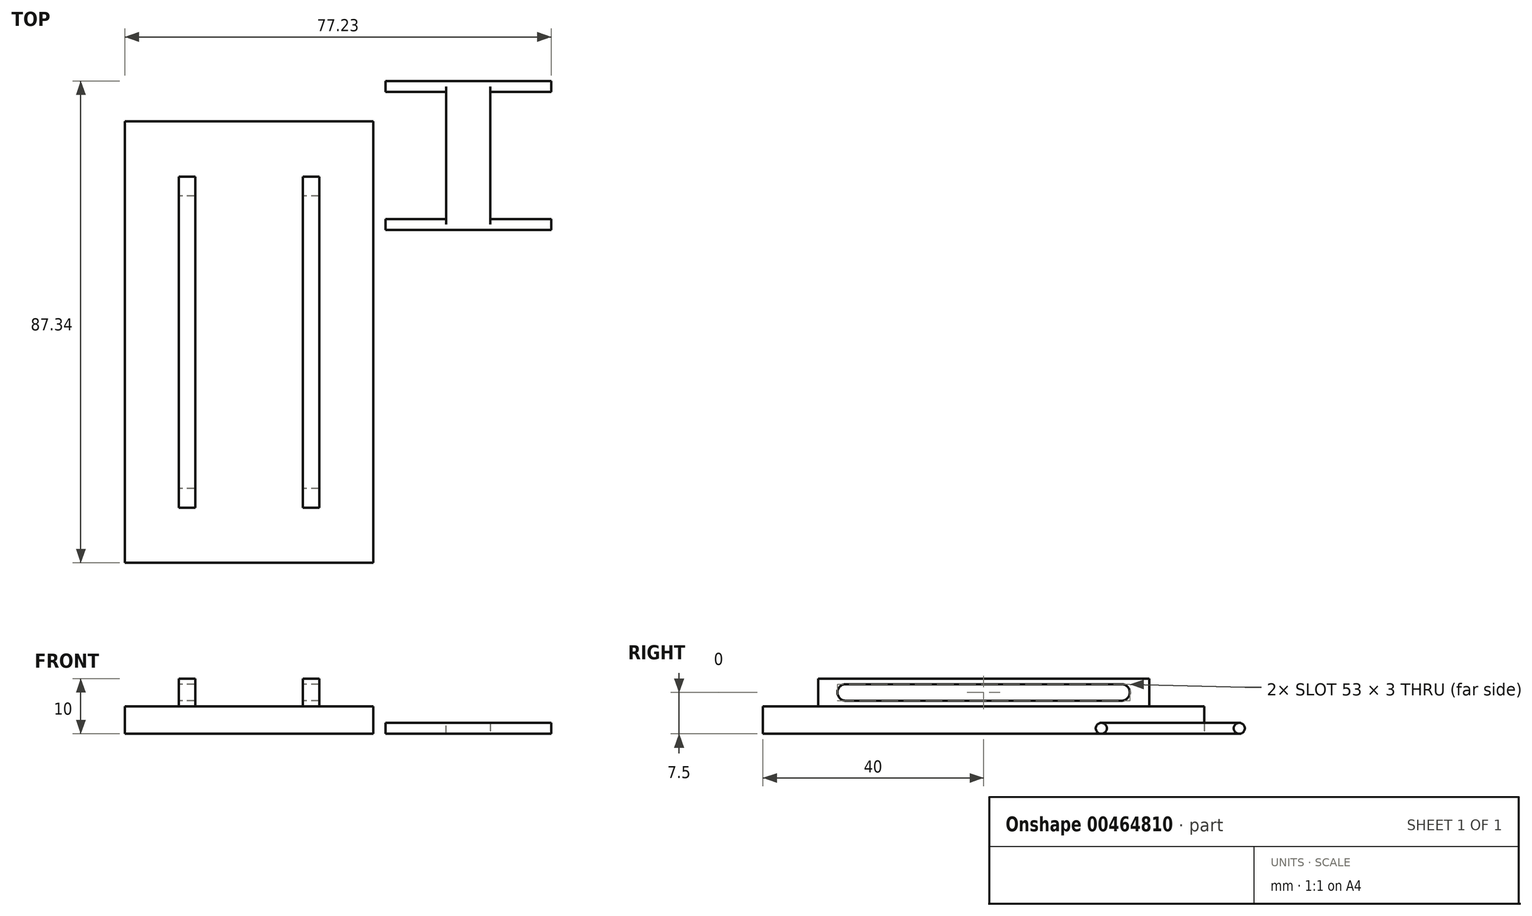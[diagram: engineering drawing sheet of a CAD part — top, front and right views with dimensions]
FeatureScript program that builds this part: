
annotation { "Feature Type Name" : "Feature", "Feature Type Description" : "" }
export const myFeature = defineFeature(function(context is Context, id is Id, definition is map)
    precondition{}
    {
        {
            var Q0;
            Q0=qCreatedBy(makeId("Top.planeOp"),FACE);
            var sketch = newSketch(context, id + "F0", { "sketchPlane" : qUnion([Q0])});
            skLineSegment(sketch, "E0.bottom", {"start": v(22.5, 40) * mm, "end": v(-22.5, 40) * mm});
            skLineSegment(sketch, "E0.top", {"start": v(22.5, -40) * mm, "end": v(-22.5, -40) * mm});
            skLineSegment(sketch, "E0.left", {"start": v(22.5, 40) * mm, "end": v(22.5, -40) * mm});
            skLineSegment(sketch, "E0.right", {"start": v(-22.5, 40) * mm, "end": v(-22.5, -40) * mm});
            skPoint(sketch, "E0.middle", {"position": v(0, 0) * mm});
            skSolve(sketch);
        }
        {
            var Q0;
            Q0=makeQuery(id+"F0.imprint","IMPRINT",FACE,{"disambiguationData":[TD([[makeQuery(id+"F0.imprint","IMPRINT",EDGE,{"derivedFrom":sQuery(id+"F0.wireOp",EDGE,"E0.bottom")}),1.0]])]});
            extrude(context, id + "F1", {"entities" : qUnion([Q0]), "depth" : 5 * mm});
        }
        {
            var Q0;
            Q0=makeQuery(id+"F1.opExtrude","CAP_FACE",FACE,{"disambiguationData":[OSD([sQuery(id+"F0.wireOp",EDGE,"E0.bottom"),sQuery(id+"F0.wireOp",EDGE,"E0.top"),sQuery(id+"F0.wireOp",EDGE,"E0.left"),sQuery(id+"F0.wireOp",EDGE,"E0.right")])],"isStart":false});
            var sketch = newSketch(context, id + "F2", { "sketchPlane" : qUnion([Q0])});
            skLineSegment(sketch, "E1", {"start": v(0, 0) * mm, "end": v(-22.5, 0) * mm, "construction": true});
            skPoint(sketch, "E2", {"position": v(-11.25, 0) * mm});
            skLineSegment(sketch, "E3.bottom", {"start": v(-9.75, 30) * mm, "end": v(-12.75, 30) * mm});
            skLineSegment(sketch, "E3.top", {"start": v(-9.75, -30) * mm, "end": v(-12.75, -30) * mm});
            skLineSegment(sketch, "E3.left", {"start": v(-9.75, 30) * mm, "end": v(-9.75, -30) * mm});
            skLineSegment(sketch, "E3.right", {"start": v(-12.75, 30) * mm, "end": v(-12.75, -30) * mm});
            skLineSegment(sketch, "E4", {"start": v(0, 0) * mm, "end": v(0, 3.84) * mm, "construction": true});
            skLineSegment(sketch, "E5.MirrorCS", {"start": v(9.75, 30) * mm, "end": v(9.75, -30) * mm});
            skLineSegment(sketch, "E6.MirrorCS", {"start": v(12.75, 30) * mm, "end": v(12.75, -30) * mm});
            skLineSegment(sketch, "E7.MirrorCS", {"start": v(9.75, 30) * mm, "end": v(12.75, 30) * mm});
            skLineSegment(sketch, "E8.MirrorCS", {"start": v(9.75, -30) * mm, "end": v(12.75, -30) * mm});
            skSolve(sketch);
        }
        {
            var Q0;
            Q0=makeQuery(id+"F2.imprint","IMPRINT",FACE,{"disambiguationData":[TD([[makeQuery(id+"F2.imprint","IMPRINT",EDGE,{"derivedFrom":sQuery(id+"F2.wireOp",EDGE,"E3.bottom")}),1.0]])]});
            var Q1;
            Q1=makeQuery(id+"F2.imprint","IMPRINT",FACE,{"disambiguationData":[TD([[makeQuery(id+"F2.imprint","IMPRINT",EDGE,{"derivedFrom":sQuery(id+"F2.wireOp",EDGE,"E5.MirrorCS")}),1.0]])]});
            extrude(context, id + "F3", {"entities" : qUnion([Q0, Q1]), "operationType" : NewBodyOperationType.ADD, "depth" : 5 * mm});
        }
        {
            var Q0;
            Q0=makeQuery(id+"F3.opExtrude","SWEPT_FACE",FACE,{"disambiguationData":[OSD([sQuery(id+"F2.wireOp",EDGE,"E3.right")])]});
            var sketch = newSketch(context, id + "F4", { "sketchPlane" : qUnion([Q0])});
            skLineSegment(sketch, "E9", {"start": v(-30, 7.5) * mm, "end": v(-25, 7.5) * mm, "construction": true});
            skCircle(sketch, "E10", {"center": v(-25, 7.5) * mm, "radius": 1.5 * mm});
            skLineSegment(sketch, "E11", {"start": v(-25, 7.5) * mm, "end": v(-25, 6) * mm, "construction": true});
            skLineSegment(sketch, "E12", {"start": v(-25, 6) * mm, "end": v(-25, 7.5) * mm, "construction": true});
            skLineSegment(sketch, "E13", {"start": v(-25, 7.5) * mm, "end": v(-25, 9) * mm, "construction": true});
            skLineSegment(sketch, "E14", {"start": v(0, 5) * mm, "end": v(0, 10) * mm, "construction": true});
            skLineSegment(sketch, "E15", {"start": v(-25, 9) * mm, "end": v(0, 9) * mm});
            skLineSegment(sketch, "E16", {"start": v(-25, 6) * mm, "end": v(0, 6) * mm});
            skLineSegment(sketch, "E17.MirrorCS", {"start": v(25, 9) * mm, "end": v(0, 9) * mm});
            skLineSegment(sketch, "E18.MirrorCS", {"start": v(25, 6) * mm, "end": v(0, 6) * mm});
            skCircle(sketch, "E19.MirrorC", {"center": v(25, 7.5) * mm, "radius": 1.5 * mm});
            skSolve(sketch);
        }
        {
            var Q0;
            Q0 = qSketchRegion(id + "F4", true);
            extrude(context, id + "F5", {"entities" : qUnion([Q0]), "operationType" : NewBodyOperationType.REMOVE, "oppositeDirection" : true, "depth" : 75.3 * mm});
        }
        {
            var Q0;
            Q0=qCreatedBy(makeId("Top.planeOp"),FACE);
            var sketch = newSketch(context, id + "F6", { "sketchPlane" : qUnion([Q0])});
            skLineSegment(sketch, "E20.bottom", {"start": v(43.73, 21.34) * mm, "end": v(35.73, 21.34) * mm});
            skLineSegment(sketch, "E20.top", {"start": v(43.73, 46.34) * mm, "end": v(35.73, 46.34) * mm});
            skLineSegment(sketch, "E20.left", {"start": v(43.73, 21.34) * mm, "end": v(43.73, 46.34) * mm});
            skLineSegment(sketch, "E20.right", {"start": v(35.73, 21.34) * mm, "end": v(35.73, 46.34) * mm});
            skPoint(sketch, "E20.middle", {"position": v(39.73, 33.84) * mm});
            skSolve(sketch);
        }
        {
            var Q0;
            Q0 = qSketchRegion(id + "F6", true);
            extrude(context, id + "F7", {"entities" : qUnion([Q0]), "depth" : 2 * mm});
        }
        {
            var Q0;
            Q0=makeQuery(id+"F7.opExtrude","SWEPT_FACE",FACE,{"disambiguationData":[OSD([sQuery(id+"F6.wireOp",EDGE,"E20.left")])]});
            var sketch = newSketch(context, id + "F8", { "sketchPlane" : qUnion([Q0])});
            skCircle(sketch, "E21", {"center": v(21.34, 1) * mm, "radius": 1 * mm});
            skLineSegment(sketch, "E22", {"start": v(33.84, 2) * mm, "end": v(33.84, 0) * mm, "construction": true});
            skCircle(sketch, "E23.MirrorC", {"center": v(46.34, 1) * mm, "radius": 1 * mm});
            skSolve(sketch);
        }
        {
            var Q0;
            {var subQ1=sQuery(id+"F6.wireOp",EDGE,"E20.left");var subQ2=makeQuery(id+"F7.opExtrude","SWEPT_EDGE",EDGE,{"disambiguationData":[OSD([sQuery(id+"F6.wireOp",EDGE,"E20.bottom"),subQ1])]});Q0=makeQuery(id+"F8.imprint","IMPRINT",FACE,{"disambiguationData":[TD([[makeQuery(id+"F8.imprint","IMPRINT",EDGE,{"derivedFrom":subQ2}),-1.0]])]});}
            var Q1;
            {var subQ1=sQuery(id+"F6.wireOp",EDGE,"E20.left");var subQ2=makeQuery(id+"F7.opExtrude","SWEPT_EDGE",EDGE,{"disambiguationData":[OSD([sQuery(id+"F6.wireOp",EDGE,"E20.bottom"),subQ1])]});Q1=makeQuery(id+"F8.imprint","IMPRINT",FACE,{"disambiguationData":[TD([[makeQuery(id+"F8.imprint","IMPRINT",EDGE,{"derivedFrom":subQ2}),1.0]])]});}
            var Q2;
            {var subQ1=sQuery(id+"F6.wireOp",EDGE,"E20.left");var subQ2=makeQuery(id+"F7.opExtrude","SWEPT_EDGE",EDGE,{"disambiguationData":[OSD([sQuery(id+"F6.wireOp",EDGE,"E20.top"),subQ1])]});Q2=makeQuery(id+"F8.imprint","IMPRINT",FACE,{"disambiguationData":[TD([[makeQuery(id+"F8.imprint","IMPRINT",EDGE,{"derivedFrom":subQ2}),1.0]])]});}
            var Q3;
            {var subQ1=sQuery(id+"F6.wireOp",EDGE,"E20.left");var subQ2=makeQuery(id+"F7.opExtrude","SWEPT_EDGE",EDGE,{"disambiguationData":[OSD([sQuery(id+"F6.wireOp",EDGE,"E20.top"),subQ1])]});Q3=makeQuery(id+"F8.imprint","IMPRINT",FACE,{"disambiguationData":[TD([[makeQuery(id+"F8.imprint","IMPRINT",EDGE,{"derivedFrom":subQ2}),-1.0]])]});}
            extrude(context, id + "F9", {"entities" : qUnion([Q0, Q1, Q2, Q3]), "operationType" : NewBodyOperationType.ADD, "depth" : 11 * mm});
        }
        {
            var Q0;
            Q0=makeQuery(id+"F7.opExtrude","SWEPT_FACE",FACE,{"disambiguationData":[OSD([sQuery(id+"F6.wireOp",EDGE,"E20.right")])]});
            var sketch = newSketch(context, id + "F10", { "sketchPlane" : qUnion([Q0])});
            skLineSegment(sketch, "E24", {"start": v(-33.84, 2) * mm, "end": v(-33.84, 0) * mm, "construction": true});
            skCircle(sketch, "E25", {"center": v(-21.34, 1) * mm, "radius": 1 * mm});
            skCircle(sketch, "E26.MirrorC", {"center": v(-46.34, 1) * mm, "radius": 1 * mm});
            skSolve(sketch);
        }
        {
            var Q0;
            {var subQ1=sQuery(id+"F6.wireOp",EDGE,"E20.right");var subQ2=makeQuery(id+"F7.opExtrude","SWEPT_EDGE",EDGE,{"disambiguationData":[OSD([sQuery(id+"F6.wireOp",EDGE,"E20.top"),subQ1])]});Q0=makeQuery(id+"F10.imprint","IMPRINT",FACE,{"disambiguationData":[TD([[makeQuery(id+"F10.imprint","IMPRINT",EDGE,{"derivedFrom":subQ2}),-1.0]])]});}
            var Q1;
            {var subQ1=sQuery(id+"F6.wireOp",EDGE,"E20.right");var subQ2=makeQuery(id+"F7.opExtrude","SWEPT_EDGE",EDGE,{"disambiguationData":[OSD([sQuery(id+"F6.wireOp",EDGE,"E20.bottom"),subQ1])]});Q1=makeQuery(id+"F10.imprint","IMPRINT",FACE,{"disambiguationData":[TD([[makeQuery(id+"F10.imprint","IMPRINT",EDGE,{"derivedFrom":subQ2}),1.0]])]});}
            extrude(context, id + "F11", {"entities" : qUnion([Q0, Q1]), "operationType" : NewBodyOperationType.ADD, "endBound" : BoundingType.UP_TO_NEXT, "oppositeDirection" : true, "depth" : 25 * mm});
        }
        {
            var Q0;
            Q0 = qSketchRegion(id + "F10", true);
            extrude(context, id + "F12", {"entities" : qUnion([Q0]), "operationType" : NewBodyOperationType.ADD, "depth" : 11 * mm});
        }
    });
